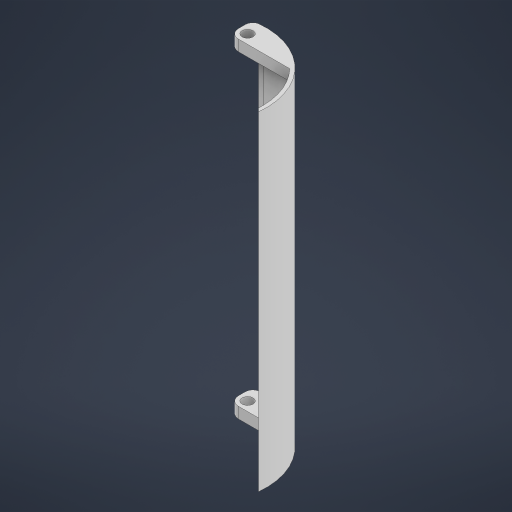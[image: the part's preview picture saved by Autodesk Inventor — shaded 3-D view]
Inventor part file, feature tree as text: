
AUTODESK INVENTOR PART (.ipt)
format: ipt  version: 2024 (Build 280153000, 153)  size: 221,696 bytes
history: native  units: mm
features: extrude x3, sketch x3, projected_geometry x2, other x1, fillet x1
ambient origin geometry x8: Origin, YZ Plane, XZ Plane, XY Plane, X Axis, Y Axis, Z Axis, Center Point
bodies: Body1 (feature_tree)
feature tree (10):
  other  "솔리드1"
  extrude  "돌출1"  Depth=25.0mm
  extrude  "돌출2"  TaperAngle=45.0deg  [1 undecoded]
  fillet  "모깎기1"  Radius=18.0mm
  extrude  "돌출3"  Depth=1.0mm
  sketch  "스케치1"
  sketch  "스케치2"
  projected_geometry  "투영된 루프1"
  sketch  "스케치3"
  projected_geometry  "투영된 루프2"
note: 1 required parameter value undecoded (feature->parameter linkage not recoverable at this tier; creation-order binding heuristic only, values carry confidence <= 0.55)
